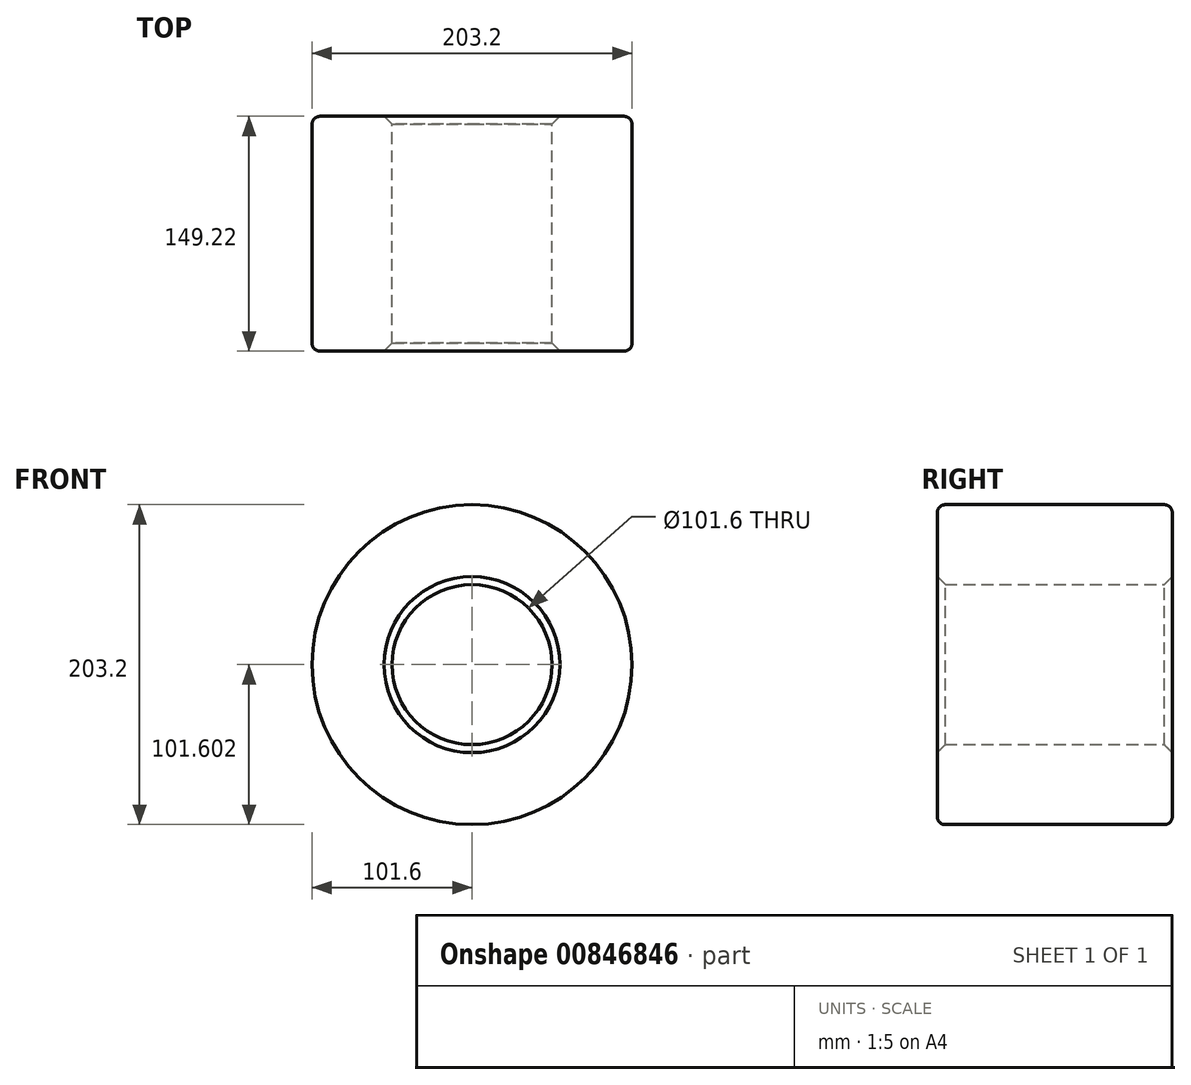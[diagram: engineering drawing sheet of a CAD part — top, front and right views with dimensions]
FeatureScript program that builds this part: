
annotation { "Feature Type Name" : "Feature", "Feature Type Description" : "" }
export const myFeature = defineFeature(function(context is Context, id is Id, definition is map)
    precondition{}
    {
        {
            var Q0;
            Q0=qCreatedBy(makeId("Front.planeOp"),FACE);
            var sketch = newSketch(context, id + "F0", { "sketchPlane" : qUnion([Q0])});
            skCircle(sketch, "E0", {"center": v(0, 9.64) * mm, "radius": 101.6 * mm});
            skCircle(sketch, "E1", {"center": v(0, 9.64) * mm, "radius": 50.8 * mm});
            skSolve(sketch);
        }
        {
            var Q0;
            Q0 = qSketchRegion(id + "F0", true);
            extrude(context, id + "F1", {"entities" : qUnion([Q0]), "depth" : 149.22 * mm, "offsetDistance" : 25.4 * mm, "symmetric" : true});
        }
        {
            var Q0;
            Q0=makeQuery(id+"F1.opExtrude","SWEPT_FACE",FACE,{"disambiguationData":[OSD([sQuery(id+"F0.wireOp",EDGE,"E0")])]});
            fillet(context, id + "F2", {"entities" : qUnion([Q0]), "radius" : 5.08 * mm, "tangentPropagation" : true, "allowEdgeOverflow" : false});
        }
        {
            var Q0;
            Q0=makeQuery(id+"F1.opExtrude","SWEPT_FACE",FACE,{"disambiguationData":[OSD([sQuery(id+"F0.wireOp",EDGE,"E1")])]});
            chamfer(context, id + "F3", {"entities" : qUnion([Q0]), "width" : 5.08 * mm, "tangentPropagation" : true});
        }
    });
